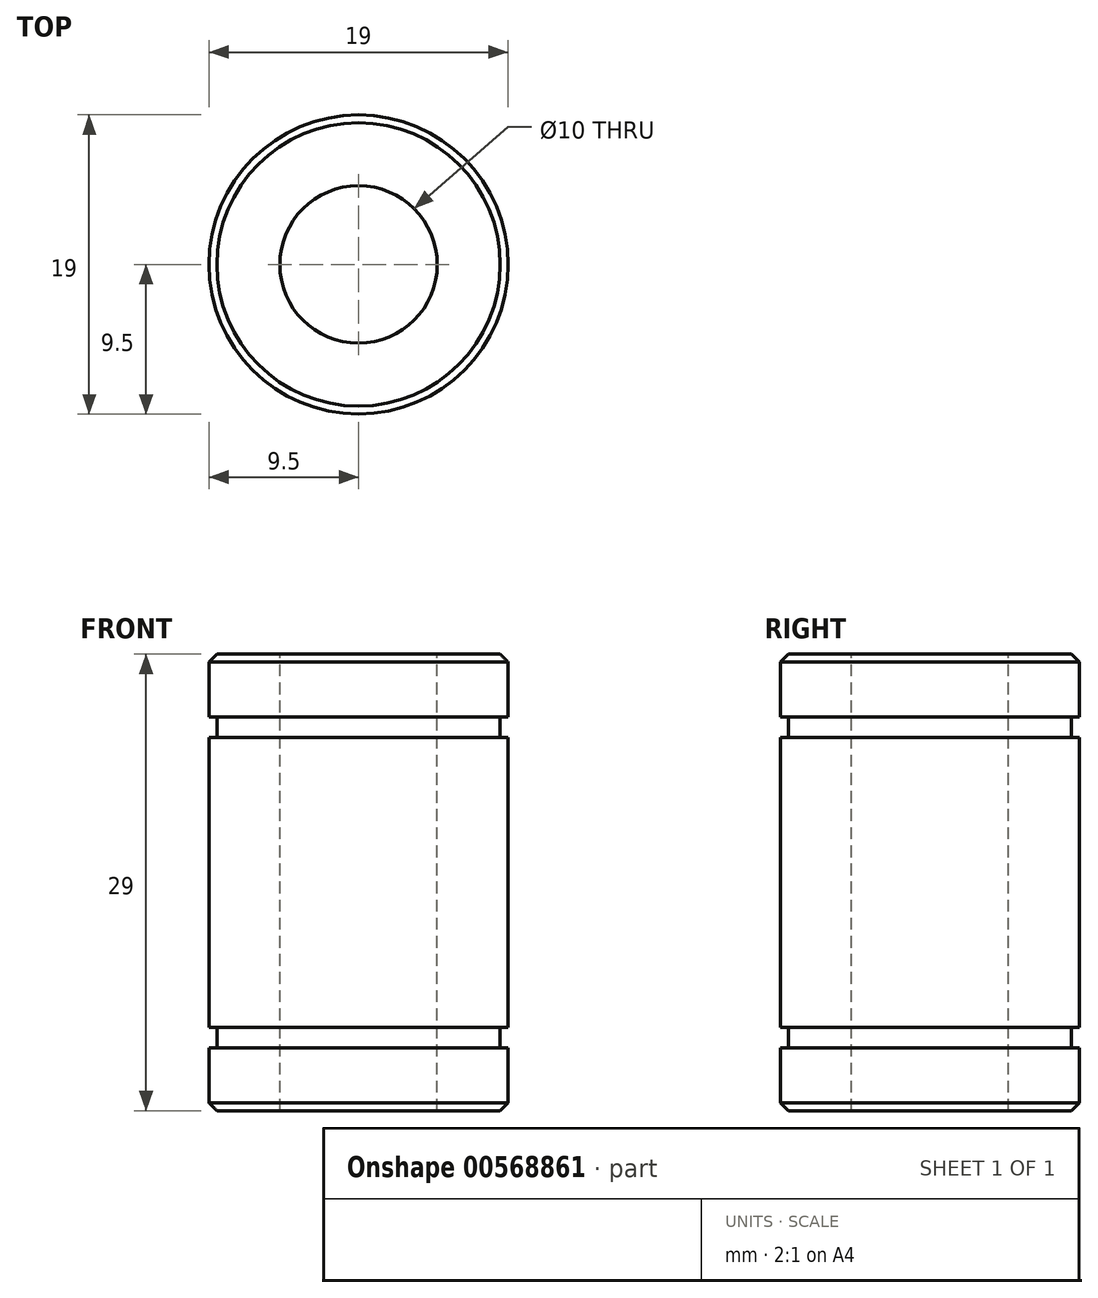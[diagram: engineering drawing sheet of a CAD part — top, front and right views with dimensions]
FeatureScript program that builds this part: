
annotation { "Feature Type Name" : "Feature", "Feature Type Description" : "" }
export const myFeature = defineFeature(function(context is Context, id is Id, definition is map)
    precondition{}
    {
        {
            var Q0;
            Q0=qCreatedBy(makeId("Front.planeOp"),FACE);
            var sketch = newSketch(context, id + "F0", { "sketchPlane" : qUnion([Q0])});
            skLineSegment(sketch, "E0", {"start": v(0, 42.47) * mm, "end": v(0, -11.66) * mm, "construction": true});
            skLineSegment(sketch, "E1", {"start": v(-9.5, 0) * mm, "end": v(-9.5, 4) * mm});
            skLineSegment(sketch, "E2", {"start": v(-9.5, 4) * mm, "end": v(-9, 4) * mm});
            skLineSegment(sketch, "E3", {"start": v(-9, 4) * mm, "end": v(-9, 5.3) * mm});
            skLineSegment(sketch, "E4", {"start": v(-9, 5.3) * mm, "end": v(-9.5, 5.3) * mm});
            skLineSegment(sketch, "E5", {"start": v(-9.5, 5.3) * mm, "end": v(-9.5, 23.7) * mm});
            skLineSegment(sketch, "E6", {"start": v(-9.5, 23.7) * mm, "end": v(-9, 23.7) * mm});
            skLineSegment(sketch, "E7", {"start": v(-9, 23.7) * mm, "end": v(-9, 25) * mm});
            skLineSegment(sketch, "E8", {"start": v(-9, 25) * mm, "end": v(-9.5, 25) * mm});
            skLineSegment(sketch, "E9", {"start": v(-9.5, 25) * mm, "end": v(-9.5, 29) * mm});
            skLineSegment(sketch, "E10", {"start": v(-9.5, 0) * mm, "end": v(-5, 0) * mm});
            skLineSegment(sketch, "E11", {"start": v(-5, 0) * mm, "end": v(-5, 29) * mm});
            skLineSegment(sketch, "E12", {"start": v(-5, 29) * mm, "end": v(-9.5, 29) * mm});
            skSolve(sketch);
        }
        {
            var Q0;
            Q0 = qSketchRegion(id + "F0", true);
            var Q1;
            Q1=sQuery(id+"F0.wireOp",EDGE,"E0");
            revolve(context, id + "F1", {"entities" : qUnion([Q0]), "axis" : qUnion([Q1]), "revolveType" : RevolveType.FULL});
        }
        {
            var Q0;
            Q0=makeQuery(id+"F1.opRevolve","SWEPT_EDGE",EDGE,{"disambiguationData":[OSD([sQuery(id+"F0.wireOp",EDGE,"E9"),sQuery(id+"F0.wireOp",EDGE,"E12")])]});
            var Q1;
            Q1=makeQuery(id+"F1.opRevolve","SWEPT_EDGE",EDGE,{"disambiguationData":[OSD([sQuery(id+"F0.wireOp",EDGE,"E1"),sQuery(id+"F0.wireOp",EDGE,"E10")])]});
            chamfer(context, id + "F2", {"entities" : qUnion([Q0, Q1]), "width" : .5 * mm, "tangentPropagation" : true});
        }
    });
